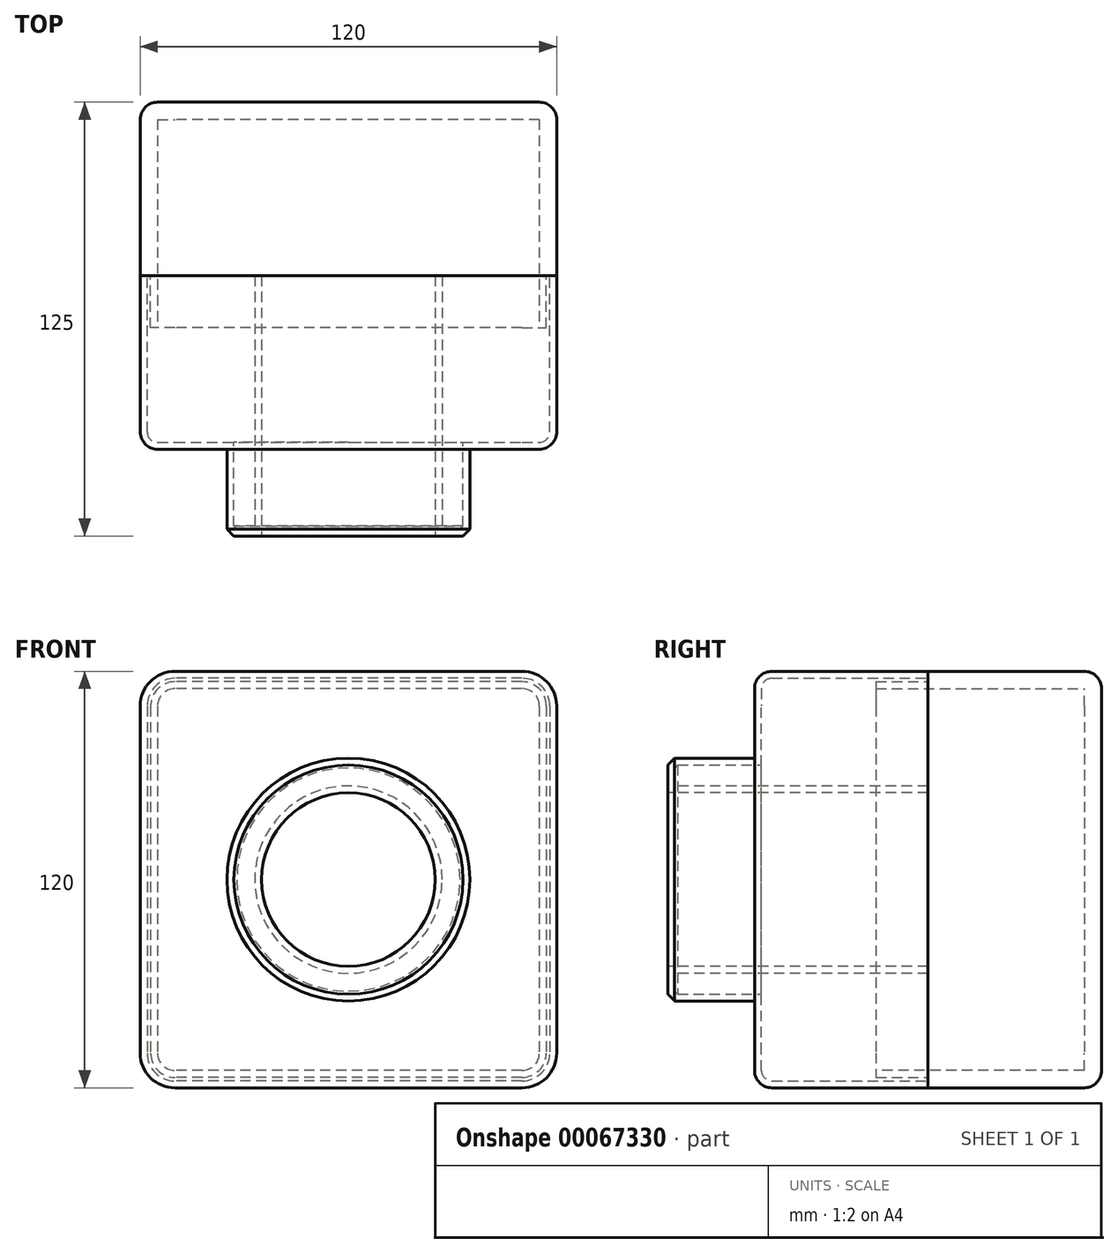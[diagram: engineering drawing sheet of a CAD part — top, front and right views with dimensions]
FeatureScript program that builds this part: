
annotation { "Feature Type Name" : "Feature", "Feature Type Description" : "" }
export const myFeature = defineFeature(function(context is Context, id is Id, definition is map)
    precondition{}
    {
        {
            var Q0;
            Q0=qCreatedBy(makeId("Front.planeOp"),FACE);
            var sketch = newSketch(context, id + "F0", { "sketchPlane" : qUnion([Q0])});
            skLineSegment(sketch, "E0.rect.bottom", {"start": v(60, 60) * mm, "end": v(-60, 60) * mm});
            skLineSegment(sketch, "E0.rect.top", {"start": v(60, -60) * mm, "end": v(-60, -60) * mm});
            skLineSegment(sketch, "E0.rect.left", {"start": v(60, 60) * mm, "end": v(60, -60) * mm});
            skLineSegment(sketch, "E0.rect.right", {"start": v(-60, 60) * mm, "end": v(-60, -60) * mm});
            skPoint(sketch, "E0.rect.middle", {"position": v(0, 0) * mm});
            skSolve(sketch);
        }
        {
            var Q0;
            Q0=makeQuery(id+"F0.imprint","IMPRINT",FACE,{"disambiguationData":[TD([[makeQuery(id+"F0.imprint","IMPRINT",EDGE,{"derivedFrom":sQuery(id+"F0.wireOp",EDGE,"E0.rect.bottom")}),1.0]])]});
            extrude(context, id + "F1", {"entities" : qUnion([Q0]), "depth" : 50 * mm});
        }
        {
            var Q0;
            Q0=makeQuery(id+"F1.opExtrude","CAP_FACE",FACE,{"disambiguationData":[OSD([sQuery(id+"F0.wireOp",EDGE,"E0.rect.bottom"),sQuery(id+"F0.wireOp",EDGE,"E0.rect.top"),sQuery(id+"F0.wireOp",EDGE,"E0.rect.left"),sQuery(id+"F0.wireOp",EDGE,"E0.rect.right")])],"isStart":false});
            var sketch = newSketch(context, id + "F2", { "sketchPlane" : qUnion([Q0])});
            skCircle(sketch, "E1", {"center": v(0, 0) * mm, "radius": 35 * mm});
            skSolve(sketch);
        }
        {
            var Q0;
            Q0 = qSketchRegion(id + "F2", true);
            extrude(context, id + "F3", {"entities" : qUnion([Q0]), "operationType" : NewBodyOperationType.ADD, "depth" : 25 * mm});
        }
        {
            var Q0;
            Q0=makeQuery(id+"F3.opExtrude","CAP_FACE",FACE,{"disambiguationData":[OSD([sQuery(id+"F2.wireOp",EDGE,"E1")])],"isStart":false});
            var sketch = newSketch(context, id + "F4", { "sketchPlane" : qUnion([Q0])});
            skCircle(sketch, "E2", {"center": v(0, 0) * mm, "radius": 25 * mm});
            skSolve(sketch);
        }
        {
            var Q0;
            Q0 = qSketchRegion(id + "F4", true);
            extrude(context, id + "F5", {"entities" : qUnion([Q0]), "operationType" : NewBodyOperationType.REMOVE, "endBound" : BoundingType.THROUGH_ALL, "oppositeDirection" : true, "depth" : 25 * mm});
        }
        {
            var Q0;
            Q0=makeQuery(id+"F1.opExtrude","SWEPT_EDGE",EDGE,{"disambiguationData":[OSD([sQuery(id+"F0.wireOp",EDGE,"E0.rect.bottom"),sQuery(id+"F0.wireOp",EDGE,"E0.rect.left")])]});
            var Q1;
            Q1=makeQuery(id+"F1.opExtrude","SWEPT_EDGE",EDGE,{"disambiguationData":[OSD([sQuery(id+"F0.wireOp",EDGE,"E0.rect.bottom"),sQuery(id+"F0.wireOp",EDGE,"E0.rect.right")])]});
            var Q2;
            Q2=makeQuery(id+"F1.opExtrude","SWEPT_EDGE",EDGE,{"disambiguationData":[OSD([sQuery(id+"F0.wireOp",EDGE,"E0.rect.top"),sQuery(id+"F0.wireOp",EDGE,"E0.rect.left")])]});
            var Q3;
            Q3=makeQuery(id+"F1.opExtrude","SWEPT_EDGE",EDGE,{"disambiguationData":[OSD([sQuery(id+"F0.wireOp",EDGE,"E0.rect.top"),sQuery(id+"F0.wireOp",EDGE,"E0.rect.right")])]});
            fillet(context, id + "F6", {"entities" : qUnion([Q0, Q1, Q2, Q3]), "radius" : 10 * mm, "tangentPropagation" : true, "allowEdgeOverflow" : false});
        }
        {
            var Q0;
            Q0=makeQuery(id+"F3.opExtrude","CAP_EDGE",EDGE,{"disambiguationData":[OSD([sQuery(id+"F2.wireOp",EDGE,"E1")])],"isStart":true});
            var Q1;
            Q1=makeQuery(id+"F1.opExtrude","CAP_EDGE",EDGE,{"disambiguationData":[OSD([sQuery(id+"F0.wireOp",EDGE,"E0.rect.bottom")])],"isStart":false});
            fillet(context, id + "F7", {"entities" : qUnion([Q0, Q1]), "radius" : 5 * mm, "tangentPropagation" : true, "allowEdgeOverflow" : false});
        }
        {
            var Q0;
            Q0=makeQuery(id+"F3.opExtrude","CAP_EDGE",EDGE,{"disambiguationData":[OSD([sQuery(id+"F2.wireOp",EDGE,"E1")])],"isStart":false});
            var Q1;
            Q1=makeQuery(id+"F5.boolean.opBoolean","COPY",EDGE,{"derivedFrom":makeQuery(id+"F5.opExtrude","CAP_EDGE",EDGE,{"disambiguationData":[OSD([sQuery(id+"F4.wireOp",EDGE,"E2")])],"isStart":true})});
            chamfer(context, id + "F8", {"entities" : qUnion([Q0, Q1]), "width" : 2 * mm, "tangentPropagation" : true});
        }
        {
            var Q0;
            Q0=makeQuery(id+"F1.opExtrude","CAP_FACE",FACE,{"disambiguationData":[OSD([sQuery(id+"F0.wireOp",EDGE,"E0.rect.bottom"),sQuery(id+"F0.wireOp",EDGE,"E0.rect.top"),sQuery(id+"F0.wireOp",EDGE,"E0.rect.left"),sQuery(id+"F0.wireOp",EDGE,"E0.rect.right")])],"isStart":true});
            shell(context, id + "F9", {"entities" : qUnion([Q0]), "thickness" : 2 * mm});
        }
        {
            var Q0;
            {var subQ0=sQuery(id+"F0.wireOp",EDGE,"E0.rect.right");var subQ1=sQuery(id+"F0.wireOp",EDGE,"E0.rect.left");var subQ2=sQuery(id+"F0.wireOp",EDGE,"E0.rect.top");var subQ3=sQuery(id+"F0.wireOp",EDGE,"E0.rect.bottom");Q0=makeQuery(id+"F9.opShell","OFFSET_FACE",FACE,{"disambiguationData":[OSD([subQ3,subQ2,subQ1,subQ0]),TDD([makeQuery(id+"F1.opExtrude","CAP_FACE",FACE,{"disambiguationData":[OSD([subQ3,subQ2,subQ1,subQ0])],"isStart":true})])]});}
            var sketch = newSketch(context, id + "F10", { "sketchPlane" : qUnion([Q0])});
            skLineSegment(sketch, "E3.0", {"start": v(-50, 60) * mm, "end": v(50, 60) * mm});
            skArc(sketch, "E3.1", {"start": v(-50, 60) * mm, "mid": v(-57.07, 57.07) * mm, "end": v(-60, 50) * mm});
            skLineSegment(sketch, "E3.2", {"start": v(-60, 50) * mm, "end": v(-60, -50) * mm});
            skArc(sketch, "E3.3", {"start": v(-60, -50) * mm, "mid": v(-57.07, -57.07) * mm, "end": v(-50, -60) * mm});
            skLineSegment(sketch, "E3.4", {"start": v(-50, -60) * mm, "end": v(50, -60) * mm});
            skArc(sketch, "E3.5", {"start": v(50, -60) * mm, "mid": v(57.07, -57.07) * mm, "end": v(60, -50) * mm});
            skLineSegment(sketch, "E3.6", {"start": v(60, 50) * mm, "end": v(60, -50) * mm});
            skArc(sketch, "E3.7", {"start": v(60, 50) * mm, "mid": v(57.07, 57.07) * mm, "end": v(50, 60) * mm});
            skSolve(sketch);
        }
        {
            var Q0;
            Q0 = qSketchRegion(id + "F10", true);
            extrude(context, id + "F11", {"entities" : qUnion([Q0]), "depth" : 50 * mm});
        }
        {
            var Q0;
            Q0=makeQuery(id+"F11.opExtrude","CAP_EDGE",EDGE,{"disambiguationData":[OSD([sQuery(id+"F10.wireOp",EDGE,"E3.2")])],"isStart":false});
            fillet(context, id + "F12", {"entities" : qUnion([Q0]), "radius" : 5 * mm, "tangentPropagation" : true, "allowEdgeOverflow" : false});
        }
        {
            var Q0;
            Q0=makeQuery(id+"F11.opExtrude","CAP_FACE",FACE,{"disambiguationData":[OSD([sQuery(id+"F10.wireOp",EDGE,"E3.0"),sQuery(id+"F10.wireOp",EDGE,"E3.1"),sQuery(id+"F10.wireOp",EDGE,"E3.2"),sQuery(id+"F10.wireOp",EDGE,"E3.3"),sQuery(id+"F10.wireOp",EDGE,"E3.4"),sQuery(id+"F10.wireOp",EDGE,"E3.5"),sQuery(id+"F10.wireOp",EDGE,"E3.6"),sQuery(id+"F10.wireOp",EDGE,"E3.7")])],"isStart":true});
            shell(context, id + "F13", {"entities" : qUnion([Q0]), "thickness" : 5 * mm});
        }
        {
            var Q0;
            Q0=makeQuery(id+"F11.opExtrude","CAP_FACE",FACE,{"disambiguationData":[OSD([sQuery(id+"F10.wireOp",EDGE,"E3.0"),sQuery(id+"F10.wireOp",EDGE,"E3.1"),sQuery(id+"F10.wireOp",EDGE,"E3.2"),sQuery(id+"F10.wireOp",EDGE,"E3.3"),sQuery(id+"F10.wireOp",EDGE,"E3.4"),sQuery(id+"F10.wireOp",EDGE,"E3.5"),sQuery(id+"F10.wireOp",EDGE,"E3.6"),sQuery(id+"F10.wireOp",EDGE,"E3.7")])],"isStart":true});
            var sketch = newSketch(context, id + "F14", { "sketchPlane" : qUnion([Q0])});
            skLineSegment(sketch, "E4.0", {"start": v(50, -55) * mm, "end": v(-50, -55) * mm});
            skArc(sketch, "E4.1", {"start": v(-50, -55) * mm, "mid": v(-53.54, -53.54) * mm, "end": v(-55, -50) * mm});
            skLineSegment(sketch, "E4.2", {"start": v(-55, 50) * mm, "end": v(-55, -50) * mm});
            skArc(sketch, "E4.3", {"start": v(-55, 50) * mm, "mid": v(-53.54, 53.54) * mm, "end": v(-50, 55) * mm});
            skLineSegment(sketch, "E4.4", {"start": v(50, 55) * mm, "end": v(-50, 55) * mm});
            skArc(sketch, "E4.5", {"start": v(50, 55) * mm, "mid": v(53.54, 53.54) * mm, "end": v(55, 50) * mm});
            skLineSegment(sketch, "E4.6", {"start": v(55, 50) * mm, "end": v(55, -50) * mm});
            skArc(sketch, "E4.7", {"start": v(55, -50) * mm, "mid": v(53.54, -53.54) * mm, "end": v(50, -55) * mm});
            skArc(sketch, "E5.0", {"start": v(-57, 50) * mm, "mid": v(-54.95, 54.95) * mm, "end": v(-50, 57) * mm});
            skLineSegment(sketch, "E5.1", {"start": v(50, 57) * mm, "end": v(-50, 57) * mm});
            skLineSegment(sketch, "E5.2", {"start": v(-57, 50) * mm, "end": v(-57, -50) * mm});
            skArc(sketch, "E5.3", {"start": v(50, 57) * mm, "mid": v(54.95, 54.95) * mm, "end": v(57, 50) * mm});
            skArc(sketch, "E5.4", {"start": v(-50, -57) * mm, "mid": v(-54.95, -54.95) * mm, "end": v(-57, -50) * mm});
            skLineSegment(sketch, "E5.5", {"start": v(50, -57) * mm, "end": v(-50, -57) * mm});
            skArc(sketch, "E5.6", {"start": v(57, -50) * mm, "mid": v(54.95, -54.95) * mm, "end": v(50, -57) * mm});
            skLineSegment(sketch, "E5.7", {"start": v(57, 50) * mm, "end": v(57, -50) * mm});
            skSolve(sketch);
        }
        {
            var Q0;
            Q0 = qSketchRegion(id + "F14", true);
            extrude(context, id + "F15", {"entities" : qUnion([Q0]), "operationType" : NewBodyOperationType.ADD, "depth" : 15 * mm});
        }
    });
